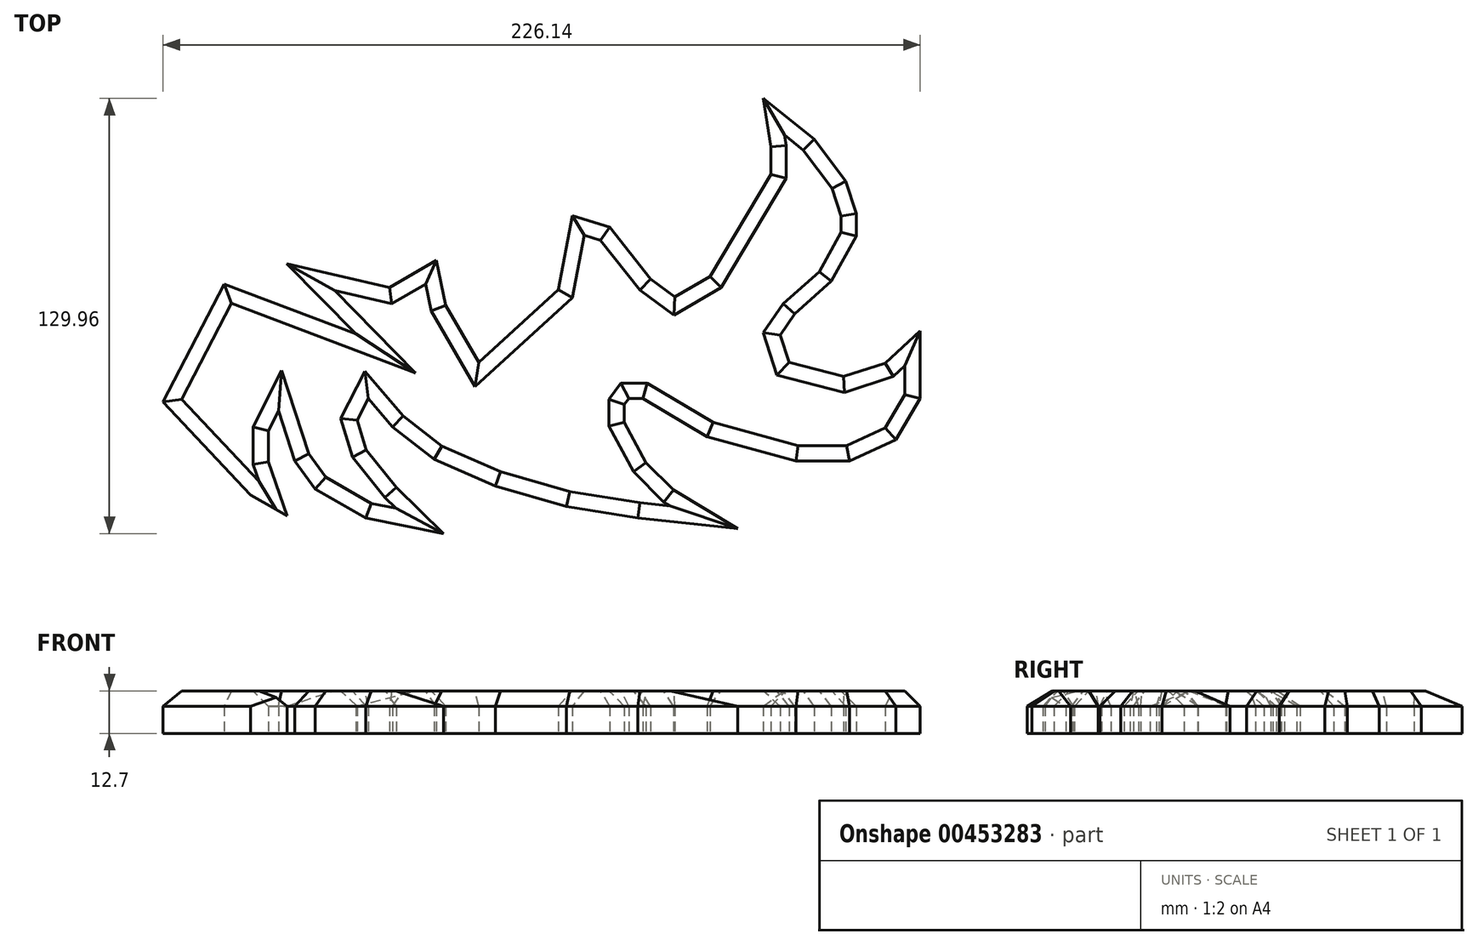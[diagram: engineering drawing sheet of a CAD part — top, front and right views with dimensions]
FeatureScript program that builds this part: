
annotation { "Feature Type Name" : "Feature", "Feature Type Description" : "" }
export const myFeature = defineFeature(function(context is Context, id is Id, definition is map)
    precondition{}
    {
        {
            var Q0;
            Q0=qCreatedBy(makeId("Top.planeOp"),FACE);
            var sketch = newSketch(context, id + "F0", { "sketchPlane" : qUnion([Q0])});
            skLineSegment(sketch, "E0", {"start": v(0, 14.36) * mm, "end": v(26.14, -13.5) * mm});
            skLineSegment(sketch, "E1", {"start": v(133.37, 66.48) * mm, "end": v(122.23, 69.89) * mm});
            skLineSegment(sketch, "E2", {"start": v(67.56, 48.44) * mm, "end": v(36.92, 55.53) * mm});
            skLineSegment(sketch, "E3", {"start": v(36.92, 55.53) * mm, "end": v(57.55, 34.57) * mm});
            skLineSegment(sketch, "E4", {"start": v(57.55, 34.57) * mm, "end": v(18.19, 49.43) * mm});
            skLineSegment(sketch, "E5", {"start": v(67.56, 48.44) * mm, "end": v(81.59, 56.54) * mm});
            skLineSegment(sketch, "E6", {"start": v(81.59, 56.54) * mm, "end": v(84.4, 43.14) * mm});
            skLineSegment(sketch, "E7", {"start": v(84.4, 43.14) * mm, "end": v(94.25, 26.05) * mm});
            skLineSegment(sketch, "E8", {"start": v(94.25, 26.05) * mm, "end": v(118, 47.77) * mm});
            skLineSegment(sketch, "E9", {"start": v(118, 47.77) * mm, "end": v(122.23, 69.89) * mm});
            skLineSegment(sketch, "E10", {"start": v(26.14, -13.5) * mm, "end": v(37.06, -19.71) * mm});
            skLineSegment(sketch, "E11", {"start": v(37.06, -19.71) * mm, "end": v(31.44, -3.65) * mm});
            skLineSegment(sketch, "E12", {"start": v(31.44, -3.65) * mm, "end": v(31.44, 5.67) * mm});
            skLineSegment(sketch, "E13", {"start": v(31.44, 5.67) * mm, "end": v(34.44, 11.69) * mm});
            skLineSegment(sketch, "E14", {"start": v(34.44, 11.69) * mm, "end": v(39.31, -3.33) * mm});
            skLineSegment(sketch, "E15", {"start": v(39.31, -3.33) * mm, "end": v(45.42, -11.68) * mm});
            skLineSegment(sketch, "E16", {"start": v(45.42, -11.68) * mm, "end": v(60.52, -20.36) * mm});
            skLineSegment(sketch, "E17", {"start": v(60.52, -20.36) * mm, "end": v(83.81, -25.01) * mm});
            skLineSegment(sketch, "E18", {"start": v(83.81, -25.01) * mm, "end": v(69.67, -11.2) * mm});
            skLineSegment(sketch, "E19", {"start": v(69.67, -11.2) * mm, "end": v(60.68, 0) * mm});
            skLineSegment(sketch, "E20", {"start": v(60.68, 0) * mm, "end": v(57.95, 8.88) * mm});
            skLineSegment(sketch, "E21", {"start": v(57.95, 8.88) * mm, "end": v(61.21, 15.27) * mm});
            skLineSegment(sketch, "E22", {"start": v(61.21, 15.27) * mm, "end": v(68.55, 6.8) * mm});
            skLineSegment(sketch, "E23", {"start": v(68.55, 6.8) * mm, "end": v(80.92, -2.85) * mm});
            skLineSegment(sketch, "E24", {"start": v(80.92, -2.85) * mm, "end": v(99.23, -10.88) * mm});
            skLineSegment(sketch, "E25", {"start": v(99.23, -10.88) * mm, "end": v(120.44, -16.98) * mm});
            skLineSegment(sketch, "E26", {"start": v(120.44, -16.98) * mm, "end": v(141.8, -20.36) * mm});
            skLineSegment(sketch, "E27", {"start": v(141.8, -20.36) * mm, "end": v(171.68, -23.57) * mm});
            skLineSegment(sketch, "E28", {"start": v(171.68, -23.57) * mm, "end": v(152.4, -12) * mm});
            skLineSegment(sketch, "E29", {"start": v(152.4, -12) * mm, "end": v(144.21, -3.8) * mm});
            skLineSegment(sketch, "E30", {"start": v(144.21, -3.8) * mm, "end": v(137.79, 8.24) * mm});
            skLineSegment(sketch, "E31", {"start": v(137.79, 8.24) * mm, "end": v(137.79, 13.54) * mm});
            skLineSegment(sketch, "E32", {"start": v(137.79, 13.54) * mm, "end": v(139.07, 15.27) * mm});
            skLineSegment(sketch, "E33", {"start": v(139.07, 15.27) * mm, "end": v(143.29, 15.27) * mm});
            skLineSegment(sketch, "E34", {"start": v(143.29, 15.27) * mm, "end": v(162.53, 3.9) * mm});
            skLineSegment(sketch, "E35", {"start": v(162.53, 3.9) * mm, "end": v(189.03, -3.33) * mm});
            skLineSegment(sketch, "E36", {"start": v(189.03, -3.33) * mm, "end": v(205.1, -3.33) * mm});
            skLineSegment(sketch, "E37", {"start": v(205.1, -3.33) * mm, "end": v(218.91, 2.94) * mm});
            skLineSegment(sketch, "E38", {"start": v(218.91, 2.94) * mm, "end": v(226.14, 15.27) * mm});
            skLineSegment(sketch, "E39", {"start": v(226.14, 15.27) * mm, "end": v(226.14, 35.55) * mm});
            skLineSegment(sketch, "E40", {"start": v(226.14, 35.55) * mm, "end": v(215.7, 25.91) * mm});
            skLineSegment(sketch, "E41", {"start": v(215.7, 25.91) * mm, "end": v(203.33, 21.9) * mm});
            skLineSegment(sketch, "E42", {"start": v(203.33, 21.9) * mm, "end": v(186.94, 26.07) * mm});
            skLineSegment(sketch, "E43", {"start": v(186.94, 26.07) * mm, "end": v(184.3, 34.23) * mm});
            skLineSegment(sketch, "E44", {"start": v(184.3, 34.23) * mm, "end": v(188.71, 40.53) * mm});
            skLineSegment(sketch, "E45", {"start": v(188.71, 40.53) * mm, "end": v(199.64, 50.33) * mm});
            skLineSegment(sketch, "E46", {"start": v(199.64, 50.33) * mm, "end": v(207.03, 63.82) * mm});
            skLineSegment(sketch, "E47", {"start": v(207.03, 63.82) * mm, "end": v(207.03, 70.57) * mm});
            skLineSegment(sketch, "E48", {"start": v(207.03, 70.57) * mm, "end": v(203.9, 80.18) * mm});
            skLineSegment(sketch, "E49", {"start": v(203.9, 80.18) * mm, "end": v(194.5, 92.74) * mm});
            skLineSegment(sketch, "E50", {"start": v(194.5, 92.74) * mm, "end": v(179.23, 104.95) * mm});
            skLineSegment(sketch, "E51", {"start": v(179.23, 104.95) * mm, "end": v(181.48, 90.49) * mm});
            skLineSegment(sketch, "E52", {"start": v(181.48, 90.49) * mm, "end": v(181.48, 82.3) * mm});
            skLineSegment(sketch, "E53", {"start": v(181.48, 82.3) * mm, "end": v(163.33, 51.77) * mm});
            skLineSegment(sketch, "E54", {"start": v(163.33, 51.77) * mm, "end": v(152.89, 45.67) * mm});
            skLineSegment(sketch, "E55", {"start": v(152.89, 45.67) * mm, "end": v(145.66, 50.97) * mm});
            skLineSegment(sketch, "E56", {"start": v(145.66, 50.97) * mm, "end": v(133.37, 66.48) * mm});
            skLineSegment(sketch, "E57", {"start": v(0, 14.36) * mm, "end": v(18.19, 49.43) * mm});
            skSolve(sketch);
        }
        {
            var Q0;
            Q0=makeQuery(id+"F0.imprint","IMPRINT",FACE,{"disambiguationData":[TD([[makeQuery(id+"F0.imprint","IMPRINT",EDGE,{"derivedFrom":sQuery(id+"F0.wireOp",EDGE,"8gzG59oq-OxTQ-FSxx-rdve-sIanwsRWyK6k")}),-1.0]])]});
            var Q1;
            Q1=makeQuery(id+"F0.imprint","IMPRINT",FACE,{"disambiguationData":[TD([[makeQuery(id+"F0.imprint","IMPRINT",EDGE,{"derivedFrom":sQuery(id+"F0.wireOp",EDGE,"RamSxRYM-kuQw-MWln-RZHq-MzstoPWcsuwb")}),1.0]])]});
            var Q2;
            Q2=makeQuery(id+"F0.imprint","IMPRINT",FACE,{"disambiguationData":[TD([[makeQuery(id+"F0.imprint","IMPRINT",EDGE,{"derivedFrom":sQuery(id+"F0.wireOp",EDGE,"YpEdwv7O-B6zP-AIVl-JrOJ-m22XQBqCcXSX")}),1.0]])]});
            var Q3;
            Q3=makeQuery(id+"F0.imprint","IMPRINT",FACE,{"disambiguationData":[TD([[makeQuery(id+"F0.imprint","IMPRINT",EDGE,{"derivedFrom":sQuery(id+"F0.wireOp",EDGE,"E0")}),1.0]])]});
            extrude(context, id + "F1", {"entities" : qUnion([Q0, Q1, Q2, Q3]), "depth" : 12.7 * mm});
        }
        {
            var Q0;
            Q0=makeQuery(id+"F1.opExtrude","CAP_FACE",FACE,{"disambiguationData":[OSD([sQuery(id+"F0.wireOp",EDGE,"8gzG59oq-OxTQ-FSxx-rdve-sIanwsRWyK6k"),sQuery(id+"F0.wireOp",EDGE,"RamSxRYM-kuQw-MWln-RZHq-MzstoPWcsuwb"),sQuery(id+"F0.wireOp",EDGE,"xXuEt2Q3-a1Rx-wnKa-WpLo-ZkFXYZCJHJvs"),sQuery(id+"F0.wireOp",EDGE,"YpEdwv7O-B6zP-AIVl-JrOJ-m22XQBqCcXSX"),sQuery(id+"F0.wireOp",EDGE,"ECiH8TIB-68ju-7HLu-BGmV-JDcuqrvO4NUZ"),sQuery(id+"F0.wireOp",EDGE,"ZpOaDlr7-NsRN-rqTp-b0f4-uZ3wF8TNIvul"),sQuery(id+"F0.wireOp",EDGE,"0wQELwE1-CWhQ-EiUJ-4uAi-mwXG0zMUX5C4"),sQuery(id+"F0.wireOp",EDGE,"lisFt2jV-1BFS-0FUr-UoKm-BeSCbLbuKbSY"),sQuery(id+"F0.wireOp",EDGE,"E0"),sQuery(id+"F0.wireOp",EDGE,"2wy2kxnH-5XdR-z53D-xJQi-JaYgUHz6AQf5"),sQuery(id+"F0.wireOp",EDGE,"3bj0mjm9-sBFO-ic1M-aFWY-6s8fHODacjw2"),sQuery(id+"F0.wireOp",EDGE,"E54m70q7-mkkY-tm5C-zSwA-sNGJN1V7RjvC"),sQuery(id+"F0.wireOp",EDGE,"L5HIFUve-NZWl-Hr0w-ss2T-ITZYmnr1ZSQo"),sQuery(id+"F0.wireOp",EDGE,"zXPXJxJq-p09I-f5Lf-kzd2-TIBfvAmG105E"),sQuery(id+"F0.wireOp",EDGE,"9APqGg2o-HuPH-3IbR-o6Ck-rxl3kNr2yTHT"),sQuery(id+"F0.wireOp",EDGE,"6viiBPzv-tAvL-oV3w-FkTQ-qZrF4OTuZlP6"),sQuery(id+"F0.wireOp",EDGE,"E1"),sQuery(id+"F0.wireOp",EDGE,"xMENqzmY-AZfS-kdv9-bNZ8-6v2j8awkabzR"),sQuery(id+"F0.wireOp",EDGE,"E2"),sQuery(id+"F0.wireOp",EDGE,"E3"),sQuery(id+"F0.wireOp",EDGE,"E4"),sQuery(id+"F0.wireOp",EDGE,"NgDZBzSB-1yjU-UK9r-4ZwU-bnzJzVYxZ6EA"),sQuery(id+"F0.wireOp",EDGE,"eeZMqTuR-89U7-AElu-AI6a-bKe9AQKogQWc"),sQuery(id+"F0.wireOp",EDGE,"Z0t5l4Pr-1eJC-4Ktx-fYmh-f8qiMCjRKOkR"),sQuery(id+"F0.wireOp",EDGE,"MyLogmMG-Wiid-Z4md-R6k0-Eu8YRH1X6ULN"),sQuery(id+"F0.wireOp",EDGE,"6Xo7Hq1z-vEPb-8VEM-74G6-T1u6vC4kKHp6")])],"isStart":false});
            chamfer(context, id + "F2", {"entities" : qUnion([Q0]), "width" : 4.57 * mm, "tangentPropagation" : true});
        }
    });
